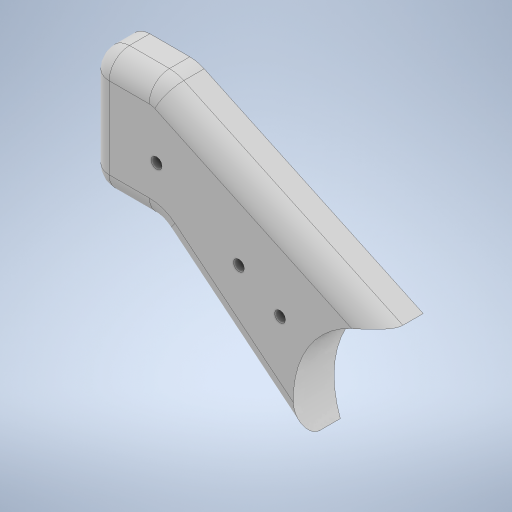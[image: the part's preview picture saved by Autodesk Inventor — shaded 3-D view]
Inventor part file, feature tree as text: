
AUTODESK INVENTOR PART (.ipt)
format: ipt  version: 2024.2 (Build 282272000, 272)  size: 351,232 bytes
history: native  units: mm
features: fillet x3, extrude x1, sketch x1
ambient origin geometry x8: Origin, YZ Plane, XZ Plane, XY Plane, X Axis, Y Axis, Z Axis, Center Point
bodies: Body1 (feature_tree)
feature tree (5):
  extrude  "Wyciągnięcie proste3"  Depth=25.0mm
  fillet  "Zaokrąglenie4"  Radius=29.0mm
  fillet  "Zaokrąglenie6"  Radius=8.0mm
  fillet  "Zaokrąglenie8"  Radius=40.0mm
  sketch  "Szkic1"
